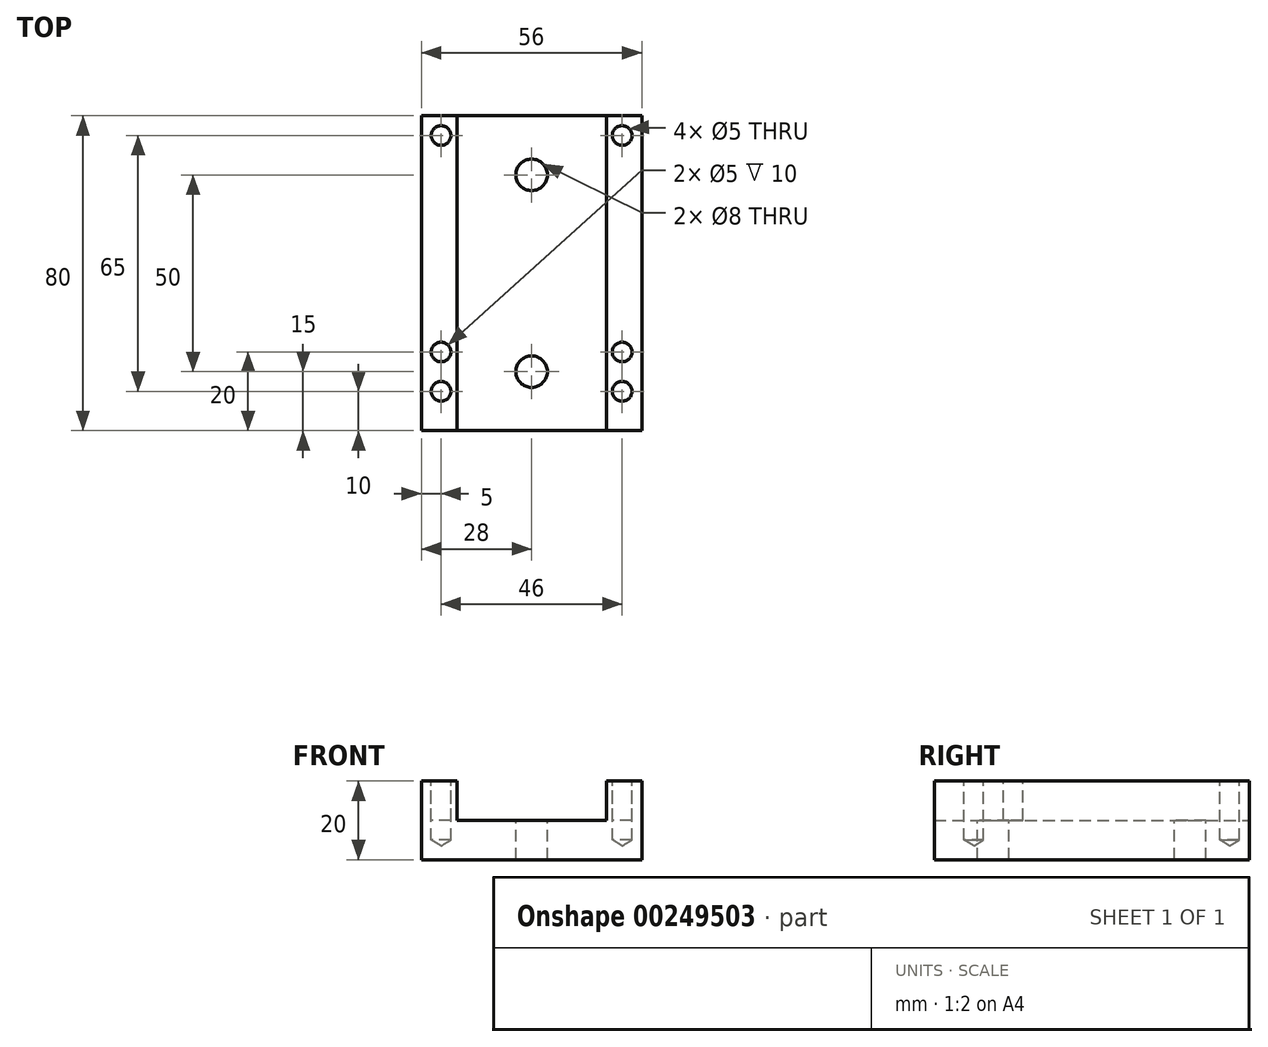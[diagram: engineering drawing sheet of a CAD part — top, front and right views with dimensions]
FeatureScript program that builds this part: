
annotation { "Feature Type Name" : "Feature", "Feature Type Description" : "" }
export const myFeature = defineFeature(function(context is Context, id is Id, definition is map)
    precondition{}
    {
        {
            var Q0;
            Q0=qCreatedBy(makeId("Front.planeOp"),FACE);
            var sketch = newSketch(context, id + "F0", { "sketchPlane" : qUnion([Q0])});
            skLineSegment(sketch, "E0.bottom", {"start": v(-28, 20) * mm, "end": v(-19, 20) * mm});
            skLineSegment(sketch, "E0.top", {"start": v(-28, 0) * mm, "end": v(28, 0) * mm});
            skLineSegment(sketch, "E0.left", {"start": v(-28, 20) * mm, "end": v(-28, 0) * mm});
            skLineSegment(sketch, "E0.right", {"start": v(28, 20) * mm, "end": v(28, 0) * mm});
            skLineSegment(sketch, "E1.top", {"start": v(-19, 10) * mm, "end": v(19, 10) * mm});
            skLineSegment(sketch, "E1.left", {"start": v(-19, 20) * mm, "end": v(-19, 10) * mm});
            skLineSegment(sketch, "E1.right", {"start": v(19, 20) * mm, "end": v(19, 10) * mm});
            skLineSegment(sketch, "E2.trimOffspring", {"start": v(19, 20) * mm, "end": v(28, 20) * mm});
            skSolve(sketch);
        }
        {
            var Q0;
            Q0 = qSketchRegion(id + "F0", true);
            extrude(context, id + "F1", {"entities" : qUnion([Q0]), "depth" : 80 * mm});
        }
        {
            var Q0;
            Q0=makeQuery(id+"F1.opExtrude","SWEPT_FACE",FACE,{"disambiguationData":[OSD([sQuery(id+"F0.wireOp",EDGE,"E2.trimOffspring")])]});
            var sketch = newSketch(context, id + "F2", { "sketchPlane" : qUnion([Q0])});
            skCircle(sketch, "E3", {"center": v(23, -60) * mm, "radius": 2.5 * mm});
            skCircle(sketch, "E4", {"center": v(-23, -60) * mm, "radius": 2.5 * mm});
            skSolve(sketch);
        }
        {
            var Q0;
            Q0 = qSketchRegion(id + "F2", true);
            extrude(context, id + "F3", {"entities" : qUnion([Q0]), "operationType" : NewBodyOperationType.REMOVE, "oppositeDirection" : true, "depth" : 10 * mm});
        }
        {
            var Q0;
            Q0=makeQuery(id+"F1.opExtrude","SWEPT_FACE",FACE,{"disambiguationData":[OSD([sQuery(id+"F0.wireOp",EDGE,"E0.bottom")])]});
            var sketch = newSketch(context, id + "F4", { "sketchPlane" : qUnion([Q0])});
            skPoint(sketch, "E5.firstSnap0", {"position": v(-23, 0) * mm});
            skLineSegment(sketch, "E5.bottom", {"start": v(-23, -5) * mm, "end": v(23, -5) * mm});
            skLineSegment(sketch, "E5.top", {"start": v(-23, -70) * mm, "end": v(23, -70) * mm});
            skLineSegment(sketch, "E5.left", {"start": v(-23, -5) * mm, "end": v(-23, -70) * mm});
            skLineSegment(sketch, "E5.right", {"start": v(23, -5) * mm, "end": v(23, -70) * mm});
            skSolve(sketch);
        }
        {
            var Q0;
            Q0=sQuery(id+"F4.wireOp",VERTEX,"E5.bottom.start");
            var Q1;
            Q1=sQuery(id+"F4.wireOp",VERTEX,"E5.right.start");
            var Q2;
            Q2=sQuery(id+"F4.wireOp",VERTEX,"E5.right.end");
            var Q3;
            Q3=sQuery(id+"F4.wireOp",VERTEX,"E5.left.end");
            var Q4;
            Q4=makeQuery(id+"F1.opExtrude","SWEPT_BODY",BODY,{"disambiguationData":[OSD([sQuery(id+"F0.wireOp",EDGE,"E0.bottom"),sQuery(id+"F0.wireOp",EDGE,"E0.top"),sQuery(id+"F0.wireOp",EDGE,"E0.left"),sQuery(id+"F0.wireOp",EDGE,"E0.right"),sQuery(id+"F0.wireOp",EDGE,"E1.top"),sQuery(id+"F0.wireOp",EDGE,"E1.left"),sQuery(id+"F0.wireOp",EDGE,"E1.right"),sQuery(id+"F0.wireOp",EDGE,"E2.trimOffspring")])]});
            hole(context, id + "F5", {"style" : HoleStyle.SIMPLE, "endStyle" : HoleEndStyle.BLIND, "standardTappedOrClearance" : lookupTablePath({ "standard" : "ISO", "engagement" : "75%", "pitch" : "1 mm", "size" : "M6", "type" : "Tapped" }), "standardBlindInLast" : lookupTablePath({ "standard" : "ISO", "engagement" : "75%", "pitch" : "1 mm", "size" : "M6", "type" : "Tapped" }), "holeDiameter" : 5 * mm, "showTappedDepth" : true, "holeDepth" : 15 * mm, "tappedDepth" : 12 * mm, "tapClearance" : 3, "startFromSketch" : true, "locations" : qUnion([Q0, Q1, Q2, Q3]), "scope" : qUnion([Q4]), "majorDiameter" : 6 * mm});
        }
        {
            var Q0;
            Q0=makeQuery(id+"F1.opExtrude","SWEPT_FACE",FACE,{"disambiguationData":[OSD([sQuery(id+"F0.wireOp",EDGE,"E1.top")])]});
            var sketch = newSketch(context, id + "F6", { "sketchPlane" : qUnion([Q0])});
            skPoint(sketch, "E6", {"position": v(0, -15) * mm});
            skPoint(sketch, "E7", {"position": v(0, -65) * mm});
            skSolve(sketch);
        }
        {
            var Q0;
            Q0=sQuery(id+"F6.wireOp",VERTEX,"E6");
            var Q1;
            Q1=sQuery(id+"F6.wireOp",VERTEX,"E7");
            var Q2;
            Q2=makeQuery(id+"F1.opExtrude","SWEPT_BODY",BODY,{"disambiguationData":[OSD([sQuery(id+"F0.wireOp",EDGE,"E0.bottom"),sQuery(id+"F0.wireOp",EDGE,"E0.top"),sQuery(id+"F0.wireOp",EDGE,"E0.left"),sQuery(id+"F0.wireOp",EDGE,"E0.right"),sQuery(id+"F0.wireOp",EDGE,"E1.top"),sQuery(id+"F0.wireOp",EDGE,"E1.left"),sQuery(id+"F0.wireOp",EDGE,"E1.right"),sQuery(id+"F0.wireOp",EDGE,"E2.trimOffspring")])]});
            hole(context, id + "F7", {"style" : HoleStyle.SIMPLE, "endStyle" : HoleEndStyle.THROUGH, "holeDiameter" : 8 * mm, "tappedDepth" : 12 * mm, "tapClearance" : 3, "startFromSketch" : true, "locations" : qUnion([Q0, Q1]), "scope" : qUnion([Q2])});
        }
    });
